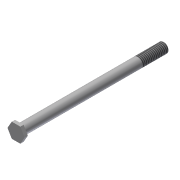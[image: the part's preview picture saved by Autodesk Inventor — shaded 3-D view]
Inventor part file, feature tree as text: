
AUTODESK INVENTOR PART (.ipt)
format: ipt  version: 2013 (Build 170138000, 138)  size: 88,576 bytes
history: native  units: in
note: dims shown in document units (in); Inventor stores cm internally (conversion verified against a paired STEP export)
features: extrude x2, sketch x2, thread x1, chamfer x1
ambient origin geometry x8: Origin, YZ Plane, XZ Plane, XY Plane, X Axis, Y Axis, Z Axis, Center Point
bodies: Solid1 (feature_tree)
feature tree (6):
  extrude  "Extrusion1"  Depth=5.5in TaperAngle=0.0deg
  extrude  "Extrusion2"  Depth=0.125in TaperAngle=0.0deg
  thread  "Thread1"  [1 undecoded]
  chamfer  "Chamfer1"  Distance=0.02in Angle=45.0deg
  sketch  "Sketch1"  dims[d0=0.375in d1=5.5in d2=0.0in]
  sketch  "Sketch2"  dims[d3=0.5625in d4=0.125in d5=0.0in d6=1.0in d7=0.0in d8=0.02in d9=0.125in d10=45.0deg]
note: 1 required parameter value undecoded (feature->parameter linkage not recoverable at this tier; creation-order binding heuristic only, values carry confidence <= 0.55)
